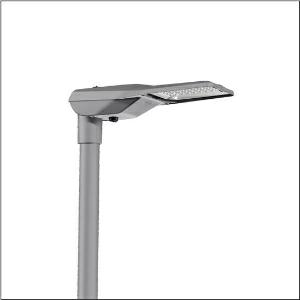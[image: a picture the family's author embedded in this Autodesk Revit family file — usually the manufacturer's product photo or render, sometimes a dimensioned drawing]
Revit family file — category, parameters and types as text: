
# Revit family: streetlight_sl_21_iq_mini___stw1_0a_5xe2e31y08hb_518f
name_source: partatom
category: Lighting Fixtures
units: mm (PartAtom-declared; Revit-internal decimal feet)

## family parameters
Cut with Voids When Loaded = No
Host = Face
Light Source = No
Part Type = Normal
Room Calculation Point = No
Round Connector Dimension = Use Diameter
Shared = No

## types (1)
- --- (1 x LED, 9750 lm, 71 W, 3000K)
    Apparent Load = 71 VA
    CIE Flux Codes = 38 75 98 100 100
    Color Rendering = 70
    Color Temperature = 3000K
    Default Elevation = 1800 mm
    Description = Streetlight SL 21 iQ mini, mast luminaire, primary light control with lens, of PMMA, primary optical cover: cover, of toughened safety glass, transparent, light distribution: STW1.0a, light emission: direct distribution, primary light characteristic: asymmetric, installation type: post-top, side-entry, LED, High Power LED, rated luminous flux: 9.750lm, luminous efficacy: 137lm/W, light colour: 730, colour temperature: 3000K, control: presetting dimming logarithmic, Street-Remote, Auto-Match, Temp-Guard, Lumen-Switch, Night-Set, Smart-Wire, Light-Fading, Desk-Remote (wireless, voltage-free reading and setting of iQ features in the workshop via application-optimized NFC function/RFID function), optimised constant luminous flux control (CLO 2.0), mains connection: 220..240V, AC, 50/60Hz, start of lifetime: 71W, end of service life: 75W, reduction: 30W, luminaire housing, of diecast aluminium, powder-coated, Siteco® metallic grey (DB 702S), corrosivity category C5 mid according to DIN EN ISO 12944, please order mast flange separately, inclination adjustable: 0°, 5°, 10°, 15°, sealing non-destructively replaceable, multi-level sealing system, length: 628mm, width: 235mm, height: 110mm, mast flange for spigot size: 42mm (side-entry): 5XC10008XM4, 60/48mm (side-entry/post-top): 5XC10108XM2, 76/60mm (side-entry/post-top): 5XC10108XM1, Smart Interface below and above, protection rating (complete): IP66, insulation class (complete): insulation class II (safety insulation), certification: CE, ENEC, ENEC+, VDE, impact resistance: IK09, permissible operating ambient temperature for outdoor applications: -40..+50°C, standard-compliant lighting for roads and squares, packaging unit: 1 piece

Light Distribution: STW1.0a
    Height = 110 mm
    Lamp = 1 x LED
    Lamp Light Flux = 9750 lm
    Lamp Power = 71 W
    Lamp count = 1
    Length = 625 mm
    Luminous efficacy = 137 lm/W
    Manufacturer = Siteco
    ModVariant = No
    Model = 5XE2E31Y08HB
    Number of Poles = 1
    OnlyDefault = Yes
    Power Factor = 1
    Product Name = Streetlight SL 21 iQ mini | STW1.0a
    Product group = mast luminaire | pylon top
    ProductGroupID = 6100
    Protection Class = Protection class II
    Protection Degree = IP 66
    RLX_Detail_Level = 1
    RLX_Emergency_Light_Flux = 0 lm
    RLX_Emergency_Type = 0
    RLX_Emergency_Type_DB = No
    RlxData = <blob elided: 92417 chars, md5=b9fcc004>
    Socket = socket
    Standby Power = 0 W
    System Light Flux = 9750 lm
    System Power = 71 W
    Type Comments = factory setting: luminous flux: 100 % | dim-lin: 254 | 716 mA
    Type Image = l_1003514.jpg
    URL = http://relux.com
    VarID = @adj_062497
    Voltage = 0 V
    Weight = 0.00 kg
    Width = 234 mm

## geometry (parser evidence)
native form markers: Blend x4, Sweep x11
no freeform markers — native parametric forms only
